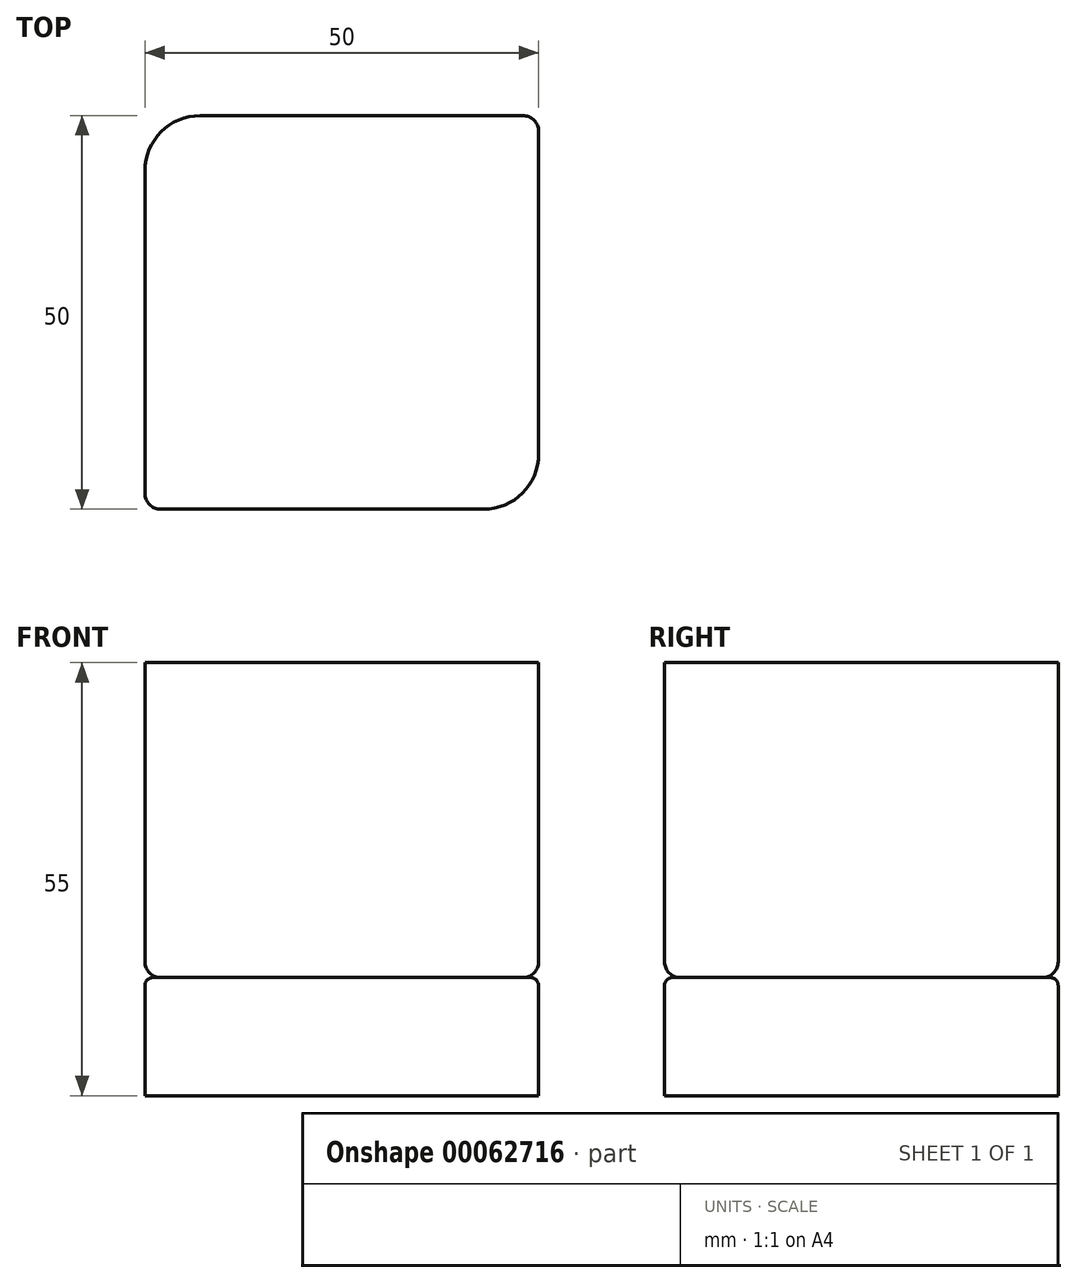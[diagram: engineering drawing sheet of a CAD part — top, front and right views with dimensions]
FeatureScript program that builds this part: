
annotation { "Feature Type Name" : "Feature", "Feature Type Description" : "" }
export const myFeature = defineFeature(function(context is Context, id is Id, definition is map)
    precondition{}
    {
        {
            var Q0;
            Q0=qCreatedBy(makeId("Top.planeOp"),FACE);
            var sketch = newSketch(context, id + "F0", { "sketchPlane" : qUnion([Q0])});
            skLineSegment(sketch, "E0.rect.bottom", {"start": v(23, 25) * mm, "end": v(-18, 25) * mm});
            skLineSegment(sketch, "E0.rect.top", {"start": v(18, -25) * mm, "end": v(-23, -25) * mm});
            skLineSegment(sketch, "E0.rect.left", {"start": v(25, 23) * mm, "end": v(25, -18) * mm});
            skLineSegment(sketch, "E0.rect.right", {"start": v(-25, 18) * mm, "end": v(-25, -23) * mm});
            skPoint(sketch, "E0.rect.middle", {"position": v(0, 0) * mm});
            skPoint(sketch, "E1.visualSharp", {"position": v(-25, 25) * mm});
            skArc(sketch, "E1.filletArc", {"start": v(-18, 25) * mm, "mid": v(-22.95, 22.95) * mm, "end": v(-25, 18) * mm});
            skPoint(sketch, "E2.visualSharp", {"position": v(25, 25) * mm});
            skArc(sketch, "E2.filletArc", {"start": v(25, 23) * mm, "mid": v(24.41, 24.41) * mm, "end": v(23, 25) * mm});
            skPoint(sketch, "E3.visualSharp", {"position": v(25, -25) * mm});
            skArc(sketch, "E3.filletArc", {"start": v(18, -25) * mm, "mid": v(22.95, -22.95) * mm, "end": v(25, -18) * mm});
            skPoint(sketch, "E4.visualSharp", {"position": v(-25, -25) * mm});
            skArc(sketch, "E4.filletArc", {"start": v(-25, -23) * mm, "mid": v(-24.41, -24.41) * mm, "end": v(-23, -25) * mm});
            skSolve(sketch);
        }
        {
            var Q0;
            Q0 = qSketchRegion(id + "F0", true);
            extrude(context, id + "F1", {"entities" : qUnion([Q0]), "depth" : 15 * mm});
        }
        {
            var Q0;
            Q0=makeQuery(id+"F1.opExtrude","CAP_FACE",FACE,{"disambiguationData":[OSD([sQuery(id+"F0.wireOp",EDGE,"E0.rect.bottom"),sQuery(id+"F0.wireOp",EDGE,"E0.rect.top"),sQuery(id+"F0.wireOp",EDGE,"E0.rect.left"),sQuery(id+"F0.wireOp",EDGE,"E0.rect.right"),sQuery(id+"F0.wireOp",EDGE,"E1.filletArc"),sQuery(id+"F0.wireOp",EDGE,"E2.filletArc"),sQuery(id+"F0.wireOp",EDGE,"E3.filletArc"),sQuery(id+"F0.wireOp",EDGE,"E4.filletArc")])],"isStart":false});
            extrude(context, id + "F2", {"entities" : qUnion([Q0]), "depth" : 40 * mm});
        }
        {
            var Q0;
            Q0=makeQuery(id+"F1.opExtrude","CAP_EDGE",EDGE,{"disambiguationData":[OSD([sQuery(id+"F0.wireOp",EDGE,"E0.rect.top")])],"isStart":false});
            var Q1;
            Q1=makeQuery(id+"F1.opExtrude","CAP_EDGE",EDGE,{"disambiguationData":[OSD([sQuery(id+"F0.wireOp",EDGE,"E3.filletArc")])],"isStart":false});
            fillet(context, id + "F3", {"entities" : qUnion([Q0, Q1]), "radius" : 1 * mm, "tangentPropagation" : true, "allowEdgeOverflow" : false});
        }
        {
            var Q0;
            Q0=makeQuery(id+"F2.opExtrude","CAP_EDGE",EDGE,{"disambiguationData":[OSD([sQuery(id+"F0.wireOp",EDGE,"E0.rect.top")])],"isStart":true});
            var Q1;
            Q1=makeQuery(id+"F2.opExtrude","CAP_EDGE",EDGE,{"disambiguationData":[OSD([sQuery(id+"F0.wireOp",EDGE,"E3.filletArc")])],"isStart":true});
            var Q2;
            Q2=makeQuery(id+"F2.opExtrude","CAP_EDGE",EDGE,{"disambiguationData":[OSD([sQuery(id+"F0.wireOp",EDGE,"E0.rect.left")])],"isStart":true});
            fillet(context, id + "F4", {"entities" : qUnion([Q0, Q1, Q2]), "radius" : 2 * mm, "tangentPropagation" : true, "allowEdgeOverflow" : false});
        }
    });
